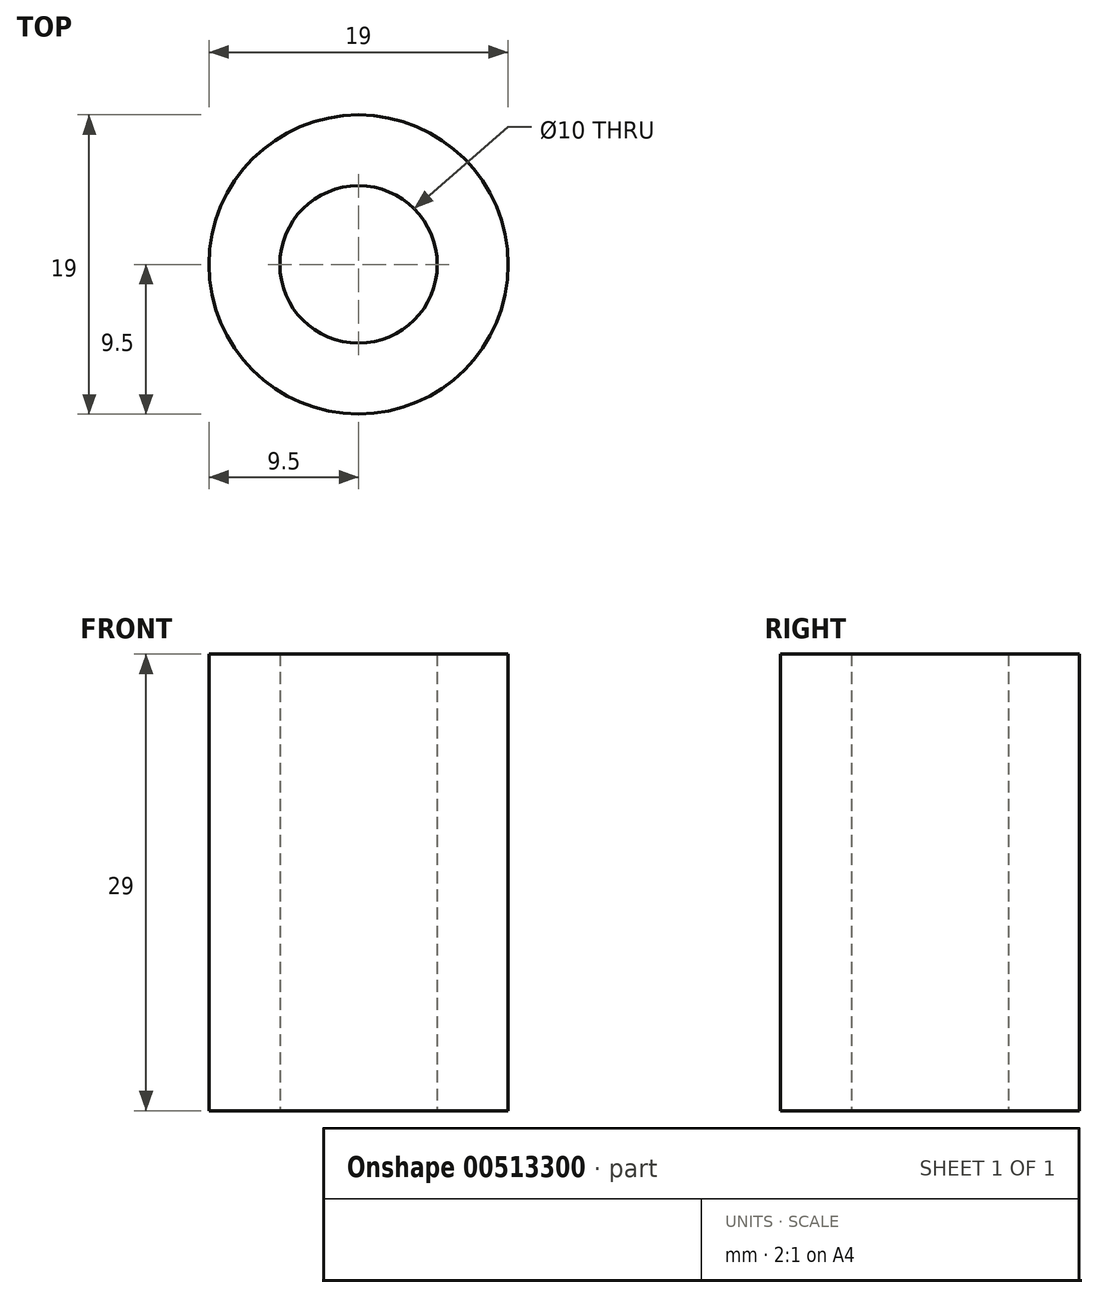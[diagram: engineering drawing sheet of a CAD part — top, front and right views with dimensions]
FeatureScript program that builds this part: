
annotation { "Feature Type Name" : "Feature", "Feature Type Description" : "" }
export const myFeature = defineFeature(function(context is Context, id is Id, definition is map)
    precondition{}
    {
        {
            var Q0;
            Q0=qCreatedBy(makeId("Top.planeOp"),FACE);
            var sketch = newSketch(context, id + "F0", { "sketchPlane" : qUnion([Q0])});
            skCircle(sketch, "E0", {"center": v(0, 0) * mm, "radius": 9.5 * mm});
            skCircle(sketch, "E1", {"center": v(0, 0) * mm, "radius": 5 * mm});
            skSolve(sketch);
        }
        {
            var Q0;
            Q0 = qSketchRegion(id + "F0", true);
            extrude(context, id + "F1", {"entities" : qUnion([Q0]), "depth" : 29 * mm, "offsetDistance" : 25 * mm});
        }
    });
